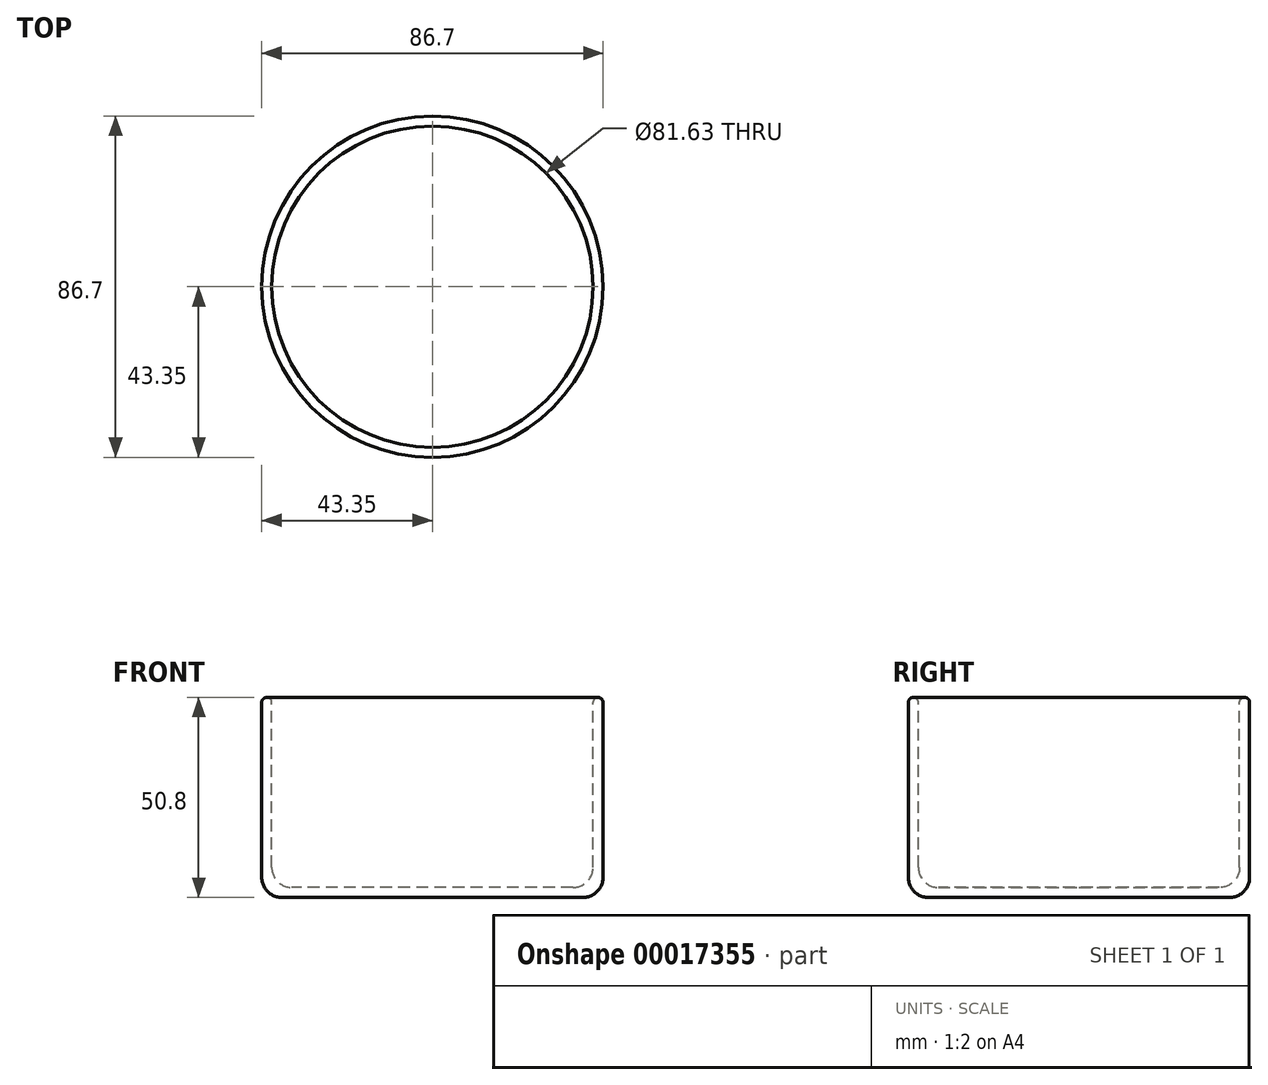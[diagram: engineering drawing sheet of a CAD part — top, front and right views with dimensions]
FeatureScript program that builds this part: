
annotation { "Feature Type Name" : "Feature", "Feature Type Description" : "" }
export const myFeature = defineFeature(function(context is Context, id is Id, definition is map)
    precondition{}
    {
        {
            var Q0;
            Q0=qCreatedBy(makeId("Top.planeOp"),FACE);
            var sketch = newSketch(context, id + "F0", { "sketchPlane" : qUnion([Q0])});
            skCircle(sketch, "E0", {"center": v(0, 0) * mm, "radius": 43.35 * mm});
            skSolve(sketch);
        }
        {
            var Q0;
            Q0 = qSketchRegion(id + "F0", true);
            extrude(context, id + "F1", {"entities" : qUnion([Q0]), "oppositeDirection" : true, "depth" : 50.8 * mm});
        }
        {
            var Q0;
            Q0=makeQuery(id+"F1.opExtrude","CAP_FACE",FACE,{"disambiguationData":[OSD([sQuery(id+"F0.wireOp",EDGE,"E0")])],"isStart":true});
            shell(context, id + "F2", {"entities" : qUnion([Q0]), "thickness" : 2.54 * mm});
        }
        {
            var Q0;
            Q0=makeQuery(id+"F1.opExtrude","CAP_EDGE",EDGE,{"disambiguationData":[OSD([sQuery(id+"F0.wireOp",EDGE,"E0")])],"isStart":true});
            var Q1;
            {var subQ0=sQuery(id+"F0.wireOp",EDGE,"E0");Q1=makeQuery(id+"F2.opShell","OFFSET_EDGE",EDGE,{"disambiguationData":[OSD([subQ0]),TDD([makeQuery(id+"F1.opExtrude","CAP_EDGE",EDGE,{"disambiguationData":[OSD([subQ0])],"isStart":true})])]});}
            fillet(context, id + "F3", {"entities" : qUnion([Q0, Q1]), "radius" : 1.27 * mm, "tangentPropagation" : true, "allowEdgeOverflow" : false});
        }
        {
            var Q0;
            Q0=makeQuery(id+"F1.opExtrude","CAP_EDGE",EDGE,{"disambiguationData":[OSD([sQuery(id+"F0.wireOp",EDGE,"E0")])],"isStart":false});
            var Q1;
            {var subQ0=sQuery(id+"F0.wireOp",EDGE,"E0");Q1=makeQuery(id+"F2.opShell","OFFSET_EDGE",EDGE,{"disambiguationData":[OSD([subQ0]),TDD([makeQuery(id+"F1.opExtrude","CAP_EDGE",EDGE,{"disambiguationData":[OSD([subQ0])],"isStart":false})])]});}
            fillet(context, id + "F4", {"entities" : qUnion([Q0, Q1]), "radius" : 5.08 * mm, "tangentPropagation" : true, "allowEdgeOverflow" : false});
        }
    });
